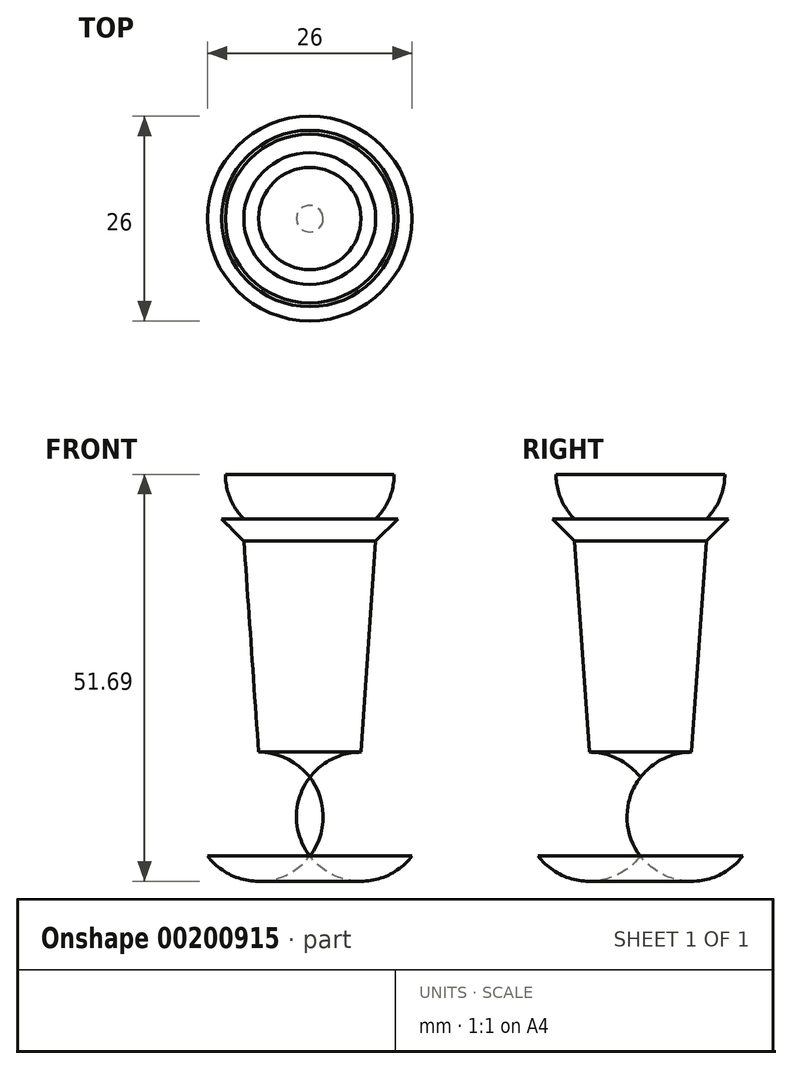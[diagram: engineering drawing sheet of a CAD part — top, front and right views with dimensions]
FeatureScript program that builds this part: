
annotation { "Feature Type Name" : "Feature", "Feature Type Description" : "" }
export const myFeature = defineFeature(function(context is Context, id is Id, definition is map)
    precondition{}
    {
        {
            var Q0;
            Q0=qCreatedBy(makeId("Front.planeOp"),FACE);
            var sketch = newSketch(context, id + "F0", { "sketchPlane" : qUnion([Q0])});
            skLineSegment(sketch, "E0", {"start": v(0, -33.92) * mm, "end": v(-13, -33.92) * mm});
            skArc(sketch, "E1", {"start": v(-13, -33.92) * mm, "mid": v(-13.86, -25.3) * mm, "end": v(-6.5, -20.72) * mm});
            skPoint(sketch, "E1.centerSnap0", {"position": v(-6.5, -33.92) * mm});
            skLineSegment(sketch, "E2", {"start": v(0, -33.92) * mm, "end": v(0, 32.35) * mm});
            skLineSegment(sketch, "E3", {"start": v(-6.5, -20.72) * mm, "end": v(-8.37, 6.08) * mm});
            skLineSegment(sketch, "E4", {"start": v(-8.37, 6.08) * mm, "end": v(-11.2, 8.91) * mm});
            skLineSegment(sketch, "E5", {"start": v(-11.2, 8.91) * mm, "end": v(-8.37, 8.91) * mm});
            skPoint(sketch, "E6.orphan", {"position": v(0, 29.85) * mm});
            skPoint(sketch, "E7.MirrorCS.start.orphan", {"position": v(8.37, 8.91) * mm});
            skPoint(sketch, "E8.MirrorCS.start.orphan", {"position": v(11.2, 8.91) * mm});
            skPoint(sketch, "E9.MirrorCS.start.orphan", {"position": v(8.37, 6.08) * mm});
            skPoint(sketch, "E10.MirrorCS.start.orphan", {"position": v(6.5, -20.72) * mm});
            skPoint(sketch, "E11.MirrorCS.start.orphan", {"position": v(13, -33.92) * mm});
            skPoint(sketch, "E12.start.orphan", {"position": v(11.48, -33.92) * mm});
            skPoint(sketch, "E13.orphan", {"position": v(0, 36.08) * mm});
            skPoint(sketch, "E14.center.orphan", {"position": v(5, 15.7) * mm});
            skLineSegment(sketch, "E15.top", {"start": v(2.94, 8.91) * mm, "end": v(0, 8.91) * mm});
            skPoint(sketch, "E15.middle", {"position": v(-2.72, 14.57) * mm});
            skPoint(sketch, "E16", {"position": v(-10.72, 14.57) * mm});
            skArc(sketch, "E17.trimOffspring", {"start": v(-10.72, 14.57) * mm, "mid": v(-10.1, 11.5) * mm, "end": v(-8.37, 8.91) * mm});
            skPoint(sketch, "E15.left.start.orphan", {"position": v(2.94, 20.23) * mm});
            skLineSegment(sketch, "E18", {"start": v(-10.72, 14.57) * mm, "end": v(0, 14.57) * mm});
            skPoint(sketch, "E18.endSnap0", {"position": v(-8.37, 14.57) * mm});
            skPoint(sketch, "E15.right.start.orphan", {"position": v(-8.37, 20.23) * mm});
            skSolve(sketch);
        }
        {
            var Q0;
            {var subQ3=sQuery(id+"F0.wireOp",EDGE,"E0");Q0=makeQuery(id+"F0.imprint","IMPRINT",FACE,{"disambiguationData":[TD([[makeQuery(id+"F0.imprint","IMPRINT",EDGE,{"derivedFrom":subQ3}),-1.0]])]});}
            var Q1;
            Q1=sQuery(id+"F0.wireOp",EDGE,"E2");
            revolve(context, id + "F1", {"entities" : qUnion([Q0]), "axis" : qUnion([Q1]), "revolveType" : RevolveType.FULL});
        }
        {
            var Q0;
            Q0=makeQuery(id+"F1.opRevolve","SWEPT_FACE",FACE,{"disambiguationData":[OSD([sQuery(id+"F0.wireOp",EDGE,"E18")])]});
            var sketch = newSketch(context, id + "F2", { "sketchPlane" : qUnion([Q0])});
            skCircle(sketch, "E19", {"center": v(0, 0) * mm, "radius": 10.72 * mm});
            skSolve(sketch);
        }
        {
            var Q0;
            Q0=makeQuery(id+"F2.imprint","IMPRINT",FACE,{"disambiguationData":[TD([[makeQuery(id+"F2.imprint","IMPRINT",EDGE,{"derivedFrom":sQuery(id+"F2.wireOp",EDGE,"E19")}),1.0]])]});
            cPlane(context, id + "F3", {"entities" : qUnion([Q0]), "cplaneType" : CPlaneType.OFFSET, "offset" : 5 * mm, "width" : 150 * mm, "height" : 150 * mm});
        }
        {
            var Q0;
            Q0=qCreatedBy(id+"F3.planeOp",FACE);
            var sketch = newSketch(context, id + "F4", { "sketchPlane" : qUnion([Q0])});
            skArc(sketch, "E20", {"start": v(-7.58, 7.58) * mm, "mid": v(0, -10.72) * mm, "end": v(7.58, 7.58) * mm});
            skLineSegment(sketch, "E21", {"start": v(-7.58, 7.58) * mm, "end": v(0, 15.16) * mm});
            skLineSegment(sketch, "E22", {"start": v(0, 15.16) * mm, "end": v(7.58, 7.58) * mm});
            skPoint(sketch, "E23.top.start.orphan", {"position": v(7.58, -7.58) * mm});
            skPoint(sketch, "E23.right.end.orphan", {"position": v(-7.58, -7.58) * mm});
            skSolve(sketch);
        }
        {
            var Q0;
            Q0=makeQuery(id+"F2.imprint","IMPRINT",FACE,{"disambiguationData":[TD([[makeQuery(id+"F2.imprint","IMPRINT",EDGE,{"derivedFrom":sQuery(id+"F2.wireOp",EDGE,"E19")}),1.0]])]});
            var sketch = newSketch(context, id + "F5", { "sketchPlane" : qUnion([Q0])});
            skLineSegment(sketch, "E24", {"start": v(-6.9, 10.72) * mm, "end": v(7.2, 10.72) * mm});
            skPoint(sketch, "E25", {"position": v(0, 10.72) * mm});
            skSolve(sketch);
        }
        {
            var Q0;
            Q0=sQuery(id+"F4.wireOp",VERTEX,"E22.start");
            var Q1;
            Q1=sQuery(id+"F5.wireOp",VERTEX,"E24.start");
            var Q2;
            Q2=sQuery(id+"F5.wireOp",VERTEX,"E24.end");
            cPlane(context, id + "F6", {"entities" : qUnion([Q0, Q1, Q2]), "cplaneType" : CPlaneType.THREE_POINT, "offset" : 25 * mm, "width" : 150 * mm, "height" : 150 * mm});
        }
    });
